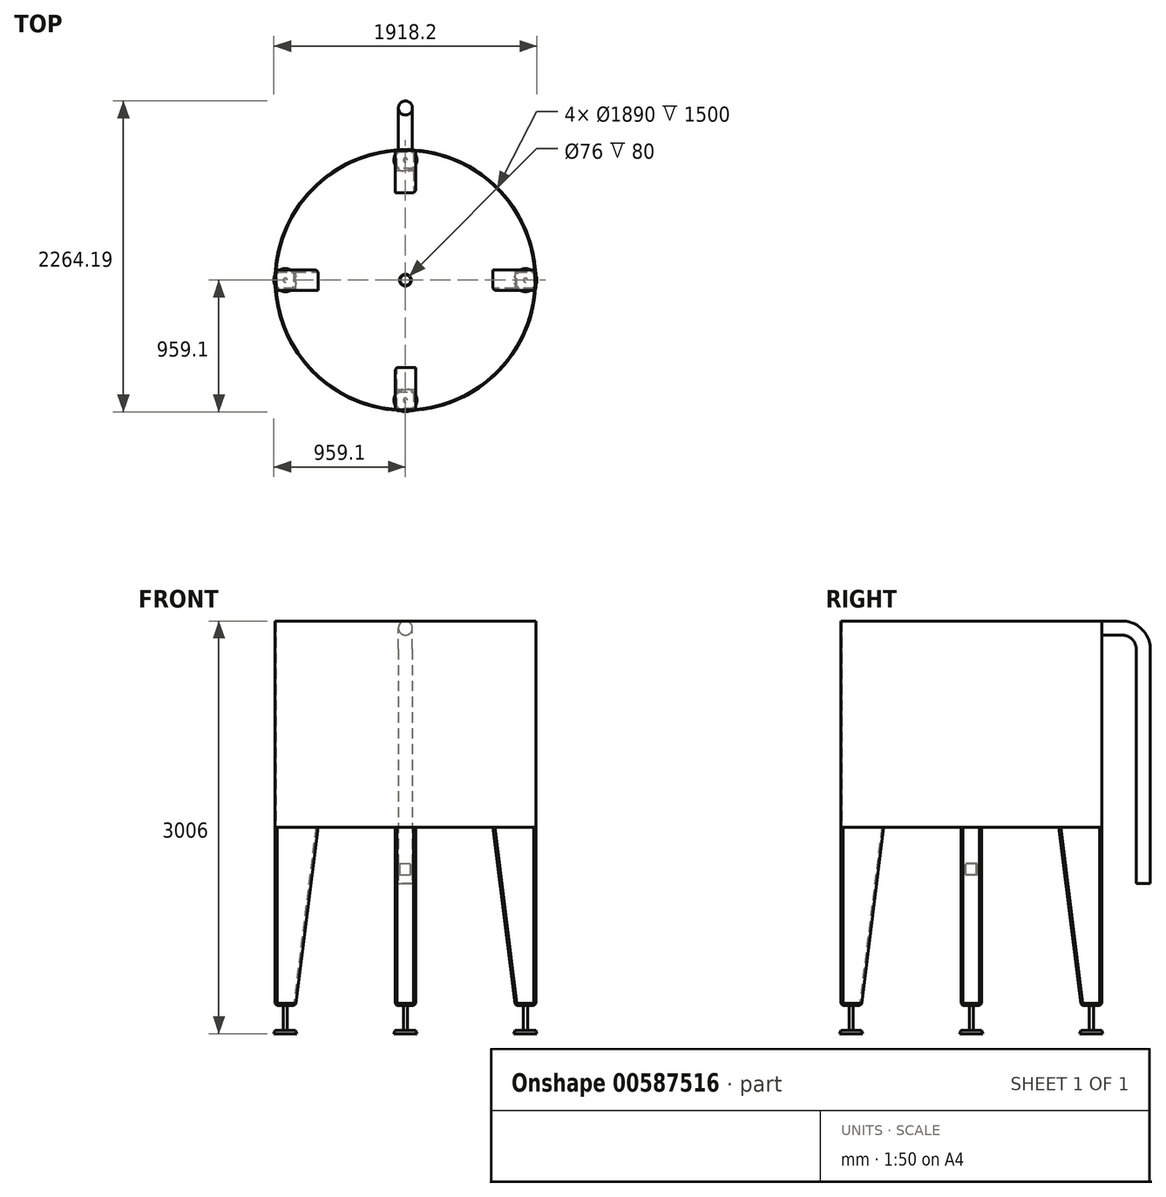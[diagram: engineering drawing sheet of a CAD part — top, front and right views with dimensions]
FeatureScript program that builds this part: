
annotation { "Feature Type Name" : "Feature", "Feature Type Description" : "" }
export const myFeature = defineFeature(function(context is Context, id is Id, definition is map)
    precondition{}
    {
        {
            var Q0;
            Q0=qCreatedBy(makeId("Top.planeOp"),FACE);
            var sketch = newSketch(context, id + "F0", { "sketchPlane" : qUnion([Q0])});
            skCircle(sketch, "E0", {"center": v(0, 0) * mm, "radius": 950 * mm});
            skCircle(sketch, "E1.0", {"center": v(0, 0) * mm, "radius": 945 * mm});
            skSolve(sketch);
        }
        {
            var Q0;
            Q0=qCreatedBy(makeId("Front.planeOp"),FACE);
            var sketch = newSketch(context, id + "F1", { "sketchPlane" : qUnion([Q0])});
            skLineSegment(sketch, "E2", {"start": v(0, 0) * mm, "end": v(0, 2123.5) * mm, "construction": true});
            skSolve(sketch);
        }
        {
            var Q0;
            Q0 = qSketchRegion(id + "F0", true);
            extrude(context, id + "F2", {"entities" : qUnion([Q0]), "depth" : 1500 * mm, "offsetDistance" : 25 * mm});
        }
        {
            var Q0;
            Q0=qCreatedBy(makeId("Front.planeOp"),FACE);
            var sketch = newSketch(context, id + "F3", { "sketchPlane" : qUnion([Q0])});
            skLineSegment(sketch, "E3", {"start": v(0, 0) * mm, "end": v(0, 1500) * mm, "construction": true});
            skLineSegment(sketch, "E4", {"start": v(950, 1500) * mm, "end": v(950, 1521.12) * mm});
            skArc(sketch, "E5", {"start": v(950, 1521.12) * mm, "mid": v(944.44, 1535.2) * mm, "end": v(930.77, 1541.68) * mm});
            skLineSegment(sketch, "E6", {"start": v(930.77, 1541.68) * mm, "end": v(93.9, 1765.91) * mm});
            skLineSegment(sketch, "E7.0", {"start": v(-950, 1500) * mm, "end": v(950, 1500) * mm, "construction": true});
            skLineSegment(sketch, "E8", {"start": v(93.9, 1765.91) * mm, "end": v(0, 1765.91) * mm});
            skLineSegment(sketch, "E9", {"start": v(0, 750) * mm, "end": v(1210.04, 750) * mm, "construction": true});
            skPoint(sketch, "E9.endSnap0", {"position": v(0, 750) * mm});
            skLineSegment(sketch, "E10.MirrorCS", {"start": v(950, 0) * mm, "end": v(950, -21.12) * mm});
            skArc(sketch, "E11.MirrorCS", {"start": v(950, -21.12) * mm, "mid": v(944.44, -35.2) * mm, "end": v(930.77, -41.68) * mm});
            skLineSegment(sketch, "E12.MirrorCS", {"start": v(930.77, -41.68) * mm, "end": v(93.9, -265.91) * mm});
            skLineSegment(sketch, "E13.MirrorCS", {"start": v(93.9, -265.91) * mm, "end": v(0, -265.91) * mm});
            skSolve(sketch);
        }
        {
            var Q0;
            Q0=sQuery(id+"F3.wireOp",EDGE,"E8");
            var Q1;
            Q1=sQuery(id+"F3.wireOp",EDGE,"E6");
            var Q2;
            Q2=sQuery(id+"F3.wireOp",EDGE,"E5");
            var Q3;
            Q3=sQuery(id+"F3.wireOp",EDGE,"E4");
            var Q4;
            Q4=sQuery(id+"F3.wireOp",EDGE,"E13.MirrorCS");
            var Q5;
            Q5=sQuery(id+"F3.wireOp",EDGE,"E12.MirrorCS");
            var Q6;
            Q6=sQuery(id+"F3.wireOp",EDGE,"E11.MirrorCS");
            var Q7;
            Q7=sQuery(id+"F3.wireOp",EDGE,"E10.MirrorCS");
            var Q8;
            Q8=sQuery(id+"F3.wireOp",EDGE,"E3");
            revolve(context, id + "F4", {"bodyType" : ExtendedToolBodyType.SURFACE, "surfaceEntities" : qUnion([Q0, Q1, Q2, Q3, Q4, Q5, Q6, Q7]), "axis" : qUnion([Q8]), "revolveType" : RevolveType.FULL});
        }
        {
            var Q0;
            Q0=qCreatedBy(makeId("Front.planeOp"),FACE);
            var sketch = newSketch(context, id + "F5", { "sketchPlane" : qUnion([Q0])});
            skLineSegment(sketch, "E14", {"start": v(1000, 0) * mm, "end": v(1000, 1383.38) * mm});
            skLineSegment(sketch, "E15", {"start": v(1000, 1383.38) * mm, "end": v(950, 1400) * mm});
            skLineSegment(sketch, "E16.0", {"start": v(-950, 1500) * mm, "end": v(950, 1500) * mm});
            skLineSegment(sketch, "E17", {"start": v(950, 1500) * mm, "end": v(950, 1400) * mm, "construction": true});
            skLineSegment(sketch, "E18", {"start": v(1000, 0) * mm, "end": v(1000, -265.91) * mm});
            skLineSegment(sketch, "E19", {"start": v(1000, -265.91) * mm, "end": v(93.9, -265.91) * mm});
            skLineSegment(sketch, "E20.0", {"start": v(-93.9, -265.91) * mm, "end": v(93.9, -265.91) * mm});
            skLineSegment(sketch, "E21", {"start": v(0, 48.74) * mm, "end": v(0, 1027) * mm, "construction": true});
            skSolve(sketch);
        }
        {
            var Q0;
            Q0=qCreatedBy(makeId("Front.planeOp"),FACE);
            var Q1;
            Q1=makeQuery(id+"F2.opExtrude","SWEPT_FACE",FACE,{"disambiguationData":[OSD([sQuery(id+"F0.wireOp",EDGE,"E0")])]});
            cPlane(context, id + "F6", {"entities" : qUnion([Q0, Q1]), "cplaneType" : CPlaneType.LINE_ANGLE, "offset" : 25 * mm, "angle" : 45 * degree, "width" : 150 * mm, "height" : 150 * mm});
        }
        {
            var Q0;
            Q0=sQuery(id+"F5.wireOp",EDGE,"E15");
            var Q1;
            Q1=sQuery(id+"F5.wireOp",EDGE,"E19");
            var Q2;
            Q2=sQuery(id+"F5.wireOp",EDGE,"E18");
            var Q3;
            Q3=sQuery(id+"F5.wireOp",EDGE,"E14");
            var Q4;
            Q4=sQuery(id+"F5.wireOp",EDGE,"E21");
            revolve(context, id + "F7", {"bodyType" : ExtendedToolBodyType.SURFACE, "surfaceEntities" : qUnion([Q0, Q1, Q2, Q3]), "axis" : qUnion([Q4]), "revolveType" : RevolveType.FULL});
        }
        {
            var Q0;
            Q0=qCreatedBy(id+"F6.planeOp",FACE);
            cPlane(context, id + "F8", {"entities" : qUnion([Q0]), "cplaneType" : CPlaneType.OFFSET, "offset" : (1900 / 2) * mm, "width" : 150 * mm, "height" : 150 * mm});
        }
        {
            var Q0;
            Q0=qCreatedBy(makeId("Top.planeOp"),FACE);
            var sketch = newSketch(context, id + "F9", { "sketchPlane" : qUnion([Q0])});
            skLineSegment(sketch, "E22", {"start": v(0, 0) * mm, "end": v(0, -1061.67) * mm, "construction": true});
            skLineSegment(sketch, "E23", {"start": v(0, 0) * mm, "end": v(1097.42, 0) * mm, "construction": true});
            skLineSegment(sketch, "E24.bottom", {"start": v(-75, -800) * mm, "end": v(75, -800) * mm});
            skLineSegment(sketch, "E24.top", {"start": v(-75, -950) * mm, "end": v(75, -950) * mm});
            skLineSegment(sketch, "E24.left", {"start": v(-75, -800) * mm, "end": v(-75, -950) * mm});
            skLineSegment(sketch, "E24.right", {"start": v(75, -800) * mm, "end": v(75, -950) * mm});
            skSolve(sketch);
        }
        {
            var Q0;
            Q0 = qSketchRegion(id + "F9", true);
            extrude(context, id + "F10", {"entities" : qUnion([Q0]), "operationType" : NewBodyOperationType.ADD, "oppositeDirection" : true, "depth" : 1300 * mm, "offsetDistance" : 25 * mm});
        }
        {
            var Q0;
            Q0=makeQuery(id+"F10.opExtrude","CAP_FACE",FACE,{"disambiguationData":[OSD([sQuery(id+"F9.wireOp",EDGE,"E24.bottom"),sQuery(id+"F9.wireOp",EDGE,"E24.top"),sQuery(id+"F9.wireOp",EDGE,"E24.left"),sQuery(id+"F9.wireOp",EDGE,"E24.right")])],"isStart":false});
            var sketch = newSketch(context, id + "F11", { "sketchPlane" : qUnion([Q0])});
            skCircle(sketch, "E25", {"center": v(0, 875) * mm, "radius": 15 * mm});
            skPoint(sketch, "E25.centerSnap0", {"position": v(-75, 875) * mm});
            skPoint(sketch, "E25.centerSnap1", {"position": v(0, 800) * mm});
            skSolve(sketch);
        }
        {
            var Q0;
            Q0 = qSketchRegion(id + "F11", true);
            extrude(context, id + "F12", {"entities" : qUnion([Q0]), "operationType" : NewBodyOperationType.ADD, "depth" : 180 * mm, "offsetDistance" : 25 * mm});
        }
        {
            var Q0;
            Q0=makeQuery(id+"F12.opExtrude","CAP_FACE",FACE,{"disambiguationData":[OSD([sQuery(id+"F11.wireOp",EDGE,"E25")])],"isStart":false});
            var sketch = newSketch(context, id + "F13", { "sketchPlane" : qUnion([Q0])});
            skCircle(sketch, "E26", {"center": v(0, 875) * mm, "radius": 75 * mm});
            skSolve(sketch);
        }
        {
            var Q0;
            Q0 = qSketchRegion(id + "F13", true);
            extrude(context, id + "F14", {"entities" : qUnion([Q0]), "operationType" : NewBodyOperationType.ADD, "depth" : 25 * mm, "offsetDistance" : 25 * mm, "hasDraft" : true, "draftAngle" : 20 * degree});
        }
        {
            var Q0;
            Q0=makeQuery(id+"F10.opExtrude","SWEPT_FACE",FACE,{"disambiguationData":[OSD([sQuery(id+"F9.wireOp",EDGE,"E24.left")])]});
            var sketch = newSketch(context, id + "F15", { "sketchPlane" : qUnion([Q0])});
            skLineSegment(sketch, "E27.0", {"start": v(800, -1300) * mm, "end": v(800, 0) * mm});
            skLineSegment(sketch, "E28", {"start": v(800, -1300) * mm, "end": v(637.57, 0) * mm});
            skLineSegment(sketch, "E29", {"start": v(637.57, 0) * mm, "end": v(800, 0) * mm});
            skSolve(sketch);
        }
        {
            var Q0;
            Q0 = qSketchRegion(id + "F15", true);
            var Q1;
            Q1=makeQuery(id+"F10.opExtrude","SWEPT_FACE",FACE,{"disambiguationData":[OSD([sQuery(id+"F9.wireOp",EDGE,"E24.right")])]});
            extrude(context, id + "F16", {"entities" : qUnion([Q0]), "operationType" : NewBodyOperationType.ADD, "endBound" : BoundingType.UP_TO_SURFACE, "oppositeDirection" : true, "depth" : 25 * mm, "endBoundEntityFace" : qUnion([Q1]), "offsetDistance" : 25 * mm});
        }
        {
            var Q0;
            Q0=makeQuery(id+"F16.opExtrude","CAP_EDGE",EDGE,{"disambiguationData":[OSD([sQuery(id+"F15.wireOp",EDGE,"E28")])],"isStart":true});
            var Q1;
            Q1=makeQuery(id+"F10.opExtrude","SWEPT_EDGE",EDGE,{"disambiguationData":[OSD([sQuery(id+"F9.wireOp",EDGE,"E24.top"),sQuery(id+"F9.wireOp",EDGE,"E24.left")])]});
            var Q2;
            Q2=makeQuery(id+"F16.opExtrude","TWEAK_EDGE",EDGE,{"derivedFrom":[makeQuery(id+"F10.opExtrude","SWEPT_FACE",FACE,{"disambiguationData":[OSD([sQuery(id+"F9.wireOp",EDGE,"E24.right")])]}),makeQuery(id+"F15.imprint","IMPRINT",EDGE,{"derivedFrom":sQuery(id+"F15.wireOp",EDGE,"E28")})]});
            var Q3;
            Q3=makeQuery(id+"F10.opExtrude","SWEPT_EDGE",EDGE,{"disambiguationData":[OSD([sQuery(id+"F9.wireOp",EDGE,"E24.top"),sQuery(id+"F9.wireOp",EDGE,"E24.right")])]});
            var Q4;
            Q4=makeQuery(id+"F10.opExtrude","CAP_EDGE",EDGE,{"disambiguationData":[OSD([sQuery(id+"F9.wireOp",EDGE,"E24.top")])],"isStart":false});
            var Q5;
            Q5=makeQuery(id+"F10.opExtrude","CAP_EDGE",EDGE,{"disambiguationData":[OSD([sQuery(id+"F9.wireOp",EDGE,"E24.left")])],"isStart":false});
            var Q6;
            Q6=makeQuery(id+"F10.opExtrude","CAP_EDGE",EDGE,{"disambiguationData":[OSD([sQuery(id+"F9.wireOp",EDGE,"E24.right")])],"isStart":false});
            var Q7;
            Q7=makeQuery(id+"F16.boolean.opBoolean","MERGE",EDGE,{"derivedFrom":[makeQuery(id+"F10.opExtrude","CAP_EDGE",EDGE,{"disambiguationData":[OSD([sQuery(id+"F9.wireOp",EDGE,"E24.bottom")])],"isStart":false}),makeQuery(id+"F16.opExtrude","SWEPT_EDGE",EDGE,{"disambiguationData":[OSD([sQuery(id+"F9.wireOp",EDGE,"E24.left"),sQuery(id+"F15.wireOp",EDGE,"E27.0"),sQuery(id+"F15.wireOp",EDGE,"E28")])]})]});
            chamfer(context, id + "F17", {"entities" : qUnion([Q0, Q1, Q2, Q3, Q4, Q5, Q6, Q7]), "width" : 15 * mm, "tangentPropagation" : true});
        }
        {
            var Q0;
            Q0=makeQuery(id+"F2.opExtrude","SWEPT_BODY",BODY,{"disambiguationData":[OSD([sQuery(id+"F0.wireOp",EDGE,"E0"),sQuery(id+"F0.wireOp",EDGE,"E1.0")])]});
            var Q1;
            Q1=makeQuery(id+"F7.opRevolve","SWEPT_FACE",FACE,{"disambiguationData":[OSD([sQuery(id+"F5.wireOp",EDGE,"E14"),sQuery(id+"F5.wireOp",EDGE,"E18")])]});
            circularPattern(context, id + "F18", {"entities" : qUnion([Q0]), "axis" : qUnion([Q1]), "angle" : 360 * degree, "instanceCount" : 4, "equalSpace" : true});
        }
        {
            var Q0;
            Q0=makeQuery(id+"F4.opRevolve","SWEPT_FACE",FACE,{"disambiguationData":[OSD([sQuery(id+"F3.wireOp",EDGE,"E13.MirrorCS")])]});
            var sketch = newSketch(context, id + "F19", { "sketchPlane" : qUnion([Q0])});
            skCircle(sketch, "E30", {"center": v(0, 0) * mm, "radius": 38 * mm});
            skCircle(sketch, "E31.0", {"center": v(0, 0) * mm, "radius": 43 * mm});
            skSolve(sketch);
        }
        {
            var Q0;
            Q0=makeQuery(id+"F4.opRevolve","SWEPT_FACE",FACE,{"disambiguationData":[OSD([sQuery(id+"F3.wireOp",EDGE,"E8")])]});
            cPlane(context, id + "F20", {"entities" : qUnion([Q0]), "cplaneType" : CPlaneType.OFFSET, "offset" : 320 * mm, "width" : 150 * mm, "height" : 150 * mm});
        }
        {
            var Q0;
            Q0=qCreatedBy(id+"F20.planeOp",FACE);
            var sketch = newSketch(context, id + "F21", { "sketchPlane" : qUnion([Q0])});
            skCircle(sketch, "E32.0", {"center": v(0, 0) * mm, "radius": 950 * mm, "construction": true});
            skSolve(sketch);
        }
        {
            var Q0;
            Q0=qCreatedBy(makeId("Right.planeOp"),FACE);
            var sketch = newSketch(context, id + "F22", { "sketchPlane" : qUnion([Q0])});
            skLineSegment(sketch, "E33", {"start": v(-950, 1445.91) * mm, "end": v(-1100, 1445.91) * mm, "construction": true});
            skArc(sketch, "E34", {"start": v(-1100, 1445.91) * mm, "mid": v(-1206.07, 1401.98) * mm, "end": v(-1250, 1295.91) * mm, "construction": true});
            skLineSegment(sketch, "E35", {"start": v(-1250, 1295.91) * mm, "end": v(-1250, -410.79) * mm, "construction": true});
            skLineSegment(sketch, "E36.MirrorCS", {"start": v(1250, 1295.91) * mm, "end": v(1250, -410.79) * mm});
            skArc(sketch, "E37.MirrorCS", {"start": v(1100, 1445.91) * mm, "mid": v(1206.07, 1401.98) * mm, "end": v(1250, 1295.91) * mm});
            skLineSegment(sketch, "E38.MirrorCS", {"start": v(950, 1445.91) * mm, "end": v(1100, 1445.91) * mm});
            skSolve(sketch);
        }
        {
            var Q0;
            Q0 = qSketchRegion(id + "F19", true);
            extrude(context, id + "F23", {"entities" : qUnion([Q0]), "depth" : 80 * mm, "offsetDistance" : 25 * mm});
        }
        {
            var Q0;
            Q0=qCreatedBy(makeId("Front.planeOp"),FACE);
            cPlane(context, id + "F24", {"entities" : qUnion([Q0]), "cplaneType" : CPlaneType.OFFSET, "offset" : (1900 / 2) * mm, "oppositeDirection" : true, "width" : 150 * mm, "height" : 150 * mm});
        }
        {
            var Q0;
            Q0=qCreatedBy(id+"F24.planeOp",FACE);
            var sketch = newSketch(context, id + "F25", { "sketchPlane" : qUnion([Q0])});
            skLineSegment(sketch, "E39", {"start": v(0, 0) * mm, "end": v(0, 2022.35) * mm, "construction": true});
            skCircle(sketch, "E40", {"center": v(0, 1450) * mm, "radius": 51 * mm});
            skSolve(sketch);
        }
        {
            var Q0;
            Q0=makeQuery(id+"F25.imprint","IMPRINT",FACE,{"disambiguationData":[TD([[makeQuery(id+"F25.imprint","IMPRINT",EDGE,{"derivedFrom":sQuery(id+"F25.wireOp",EDGE,"E40")}),1.0]])]});
            var Q1;
            Q1=sQuery(id+"F22.wireOp",EDGE,"E38.MirrorCS");
            var Q2;
            Q2=sQuery(id+"F22.wireOp",EDGE,"E37.MirrorCS");
            var Q3;
            Q3=sQuery(id+"F22.wireOp",EDGE,"E36.MirrorCS");
            sweep(context, id + "F26", {"profiles" : qUnion([Q0]), "path" : qUnion([Q1, Q2, Q3])});
        }
    });
